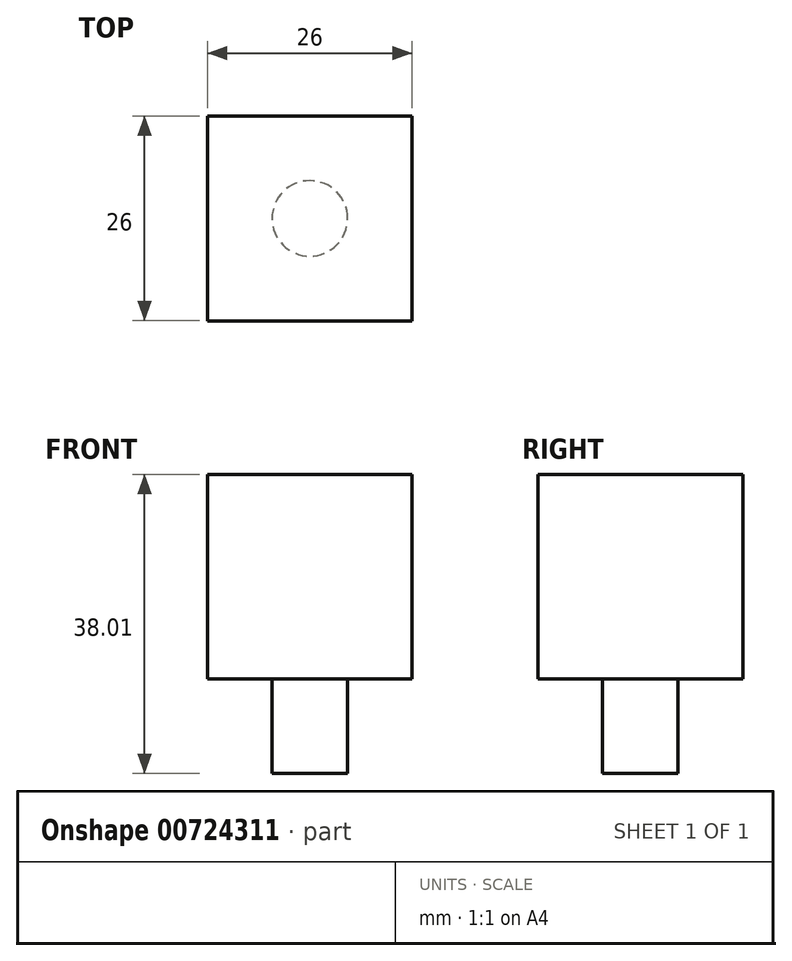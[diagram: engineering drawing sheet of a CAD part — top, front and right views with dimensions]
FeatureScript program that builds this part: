
annotation { "Feature Type Name" : "Feature", "Feature Type Description" : "" }
export const myFeature = defineFeature(function(context is Context, id is Id, definition is map)
    precondition{}
    {
        {
            var Q0;
            Q0=qCreatedBy(makeId("Top.planeOp"),FACE);
            var sketch = newSketch(context, id + "F0", { "sketchPlane" : qUnion([Q0])});
            skLineSegment(sketch, "E0.bottom", {"start": v(13, -13) * mm, "end": v(-13, -13) * mm});
            skLineSegment(sketch, "E0.top", {"start": v(13, 13) * mm, "end": v(-13, 13) * mm});
            skLineSegment(sketch, "E0.left", {"start": v(13, -13) * mm, "end": v(13, 13) * mm});
            skLineSegment(sketch, "E0.right", {"start": v(-13, -13) * mm, "end": v(-13, 13) * mm});
            skPoint(sketch, "E0.middle", {"position": v(0, 0) * mm});
            skSolve(sketch);
        }
        {
            var Q0;
            Q0 = qSketchRegion(id + "F0", true);
            extrude(context, id + "F1", {"entities" : qUnion([Q0]), "depth" : 26 * mm, "offsetDistance" : 25 * mm});
        }
        {
            var Q0;
            Q0=qCreatedBy(makeId("Top.planeOp"),FACE);
            var sketch = newSketch(context, id + "F2", { "sketchPlane" : qUnion([Q0])});
            skCircle(sketch, "E1", {"center": v(0, 0) * mm, "radius": 4.8 * mm});
            skSolve(sketch);
        }
        {
            var Q0;
            Q0 = qSketchRegion(id + "F2", true);
            extrude(context, id + "F3", {"entities" : qUnion([Q0]), "operationType" : NewBodyOperationType.ADD, "oppositeDirection" : true, "depth" : 1.2 * mm, "offsetDistance" : 25 * mm});
        }
        {
            var Q0;
            Q0 = qSketchRegion(id + "F2", true);
            extrude(context, id + "F4", {"entities" : qUnion([Q0]), "operationType" : NewBodyOperationType.ADD, "oppositeDirection" : true, "depth" : 12 * mm, "offsetDistance" : 25 * mm});
        }
    });
